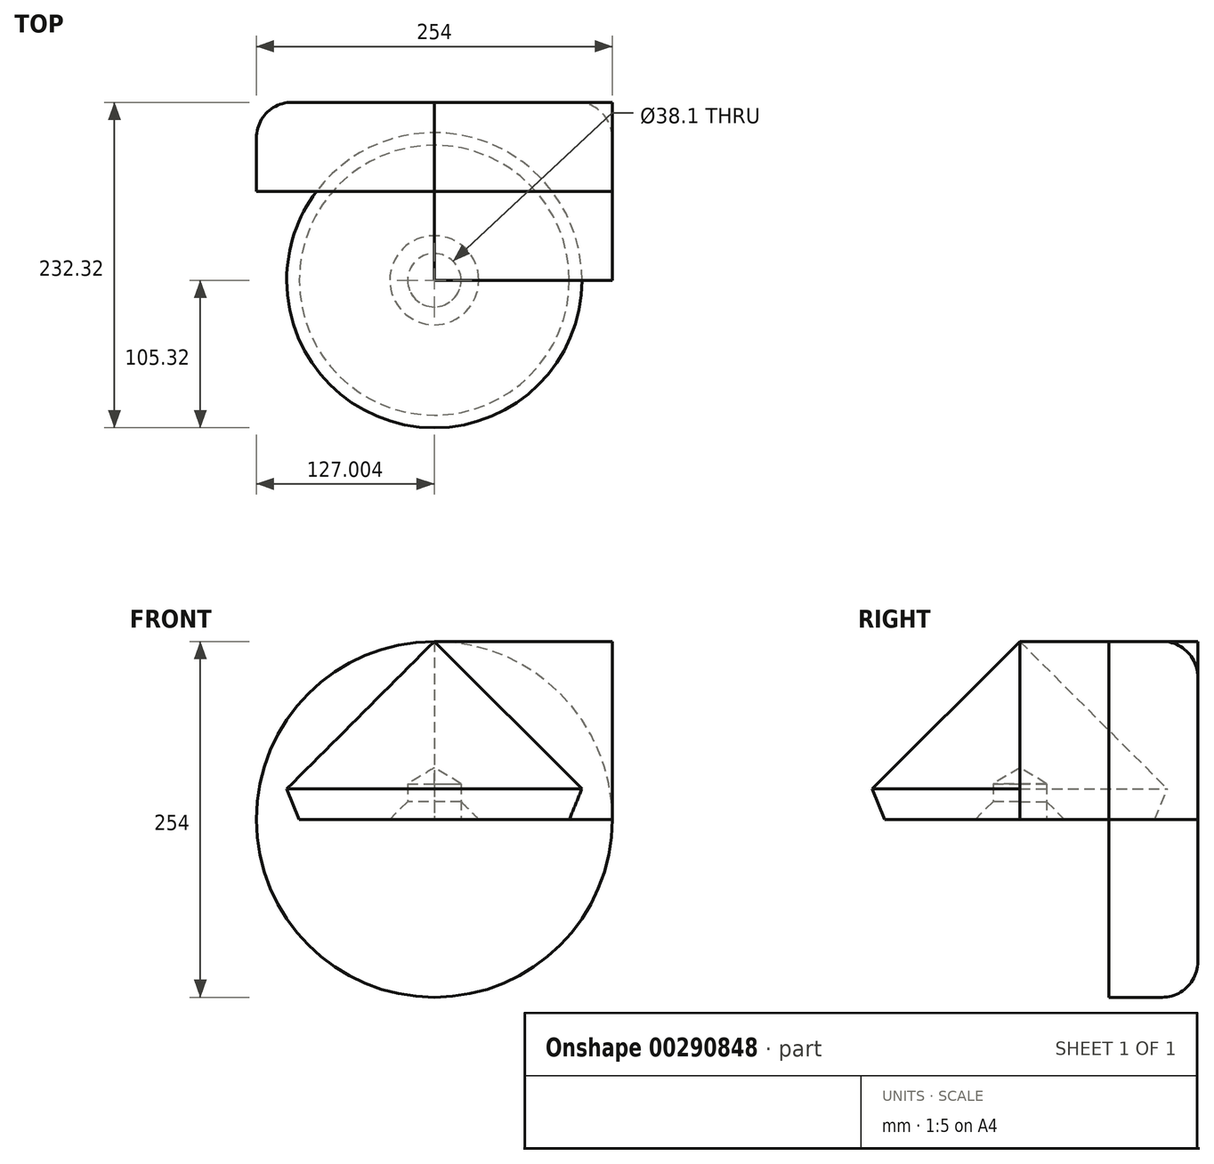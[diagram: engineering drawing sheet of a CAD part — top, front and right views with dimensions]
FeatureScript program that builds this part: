
annotation { "Feature Type Name" : "Feature", "Feature Type Description" : "" }
export const myFeature = defineFeature(function(context is Context, id is Id, definition is map)
    precondition{}
    {
        {
            var Q0;
            Q0=qCreatedBy(makeId("Front.planeOp"),FACE);
            var sketch = newSketch(context, id + "F0", { "sketchPlane" : qUnion([Q0])});
            skLineSegment(sketch, "E0.bottom", {"start": v(-69.47, 90.5) * mm, "end": v(57.53, 90.5) * mm});
            skLineSegment(sketch, "E0.top", {"start": v(-69.47, -36.5) * mm, "end": v(57.53, -36.5) * mm});
            skLineSegment(sketch, "E0.left", {"start": v(-69.47, 90.5) * mm, "end": v(-69.47, -36.5) * mm});
            skLineSegment(sketch, "E0.right", {"start": v(57.53, 90.5) * mm, "end": v(57.53, -36.5) * mm});
            skSolve(sketch);
        }
        {
            var Q0;
            Q0=makeQuery(id+"F0.imprint","IMPRINT",FACE,{"disambiguationData":[TD([[makeQuery(id+"F0.imprint","IMPRINT",EDGE,{"derivedFrom":sQuery(id+"F0.wireOp",EDGE,"E0.bottom")}),-1.0]])]});
            extrude(context, id + "F1", {"entities" : qUnion([Q0]), "depth" : 63.5 * mm, "hasSecondDirection" : true, "secondDirectionOppositeDirection" : true, "secondDirectionDepth" : 63.5 * mm});
        }
        {
            var Q0;
            Q0=makeQuery(id+"F1.opExtrude","SWEPT_FACE",FACE,{"disambiguationData":[OSD([sQuery(id+"F0.wireOp",EDGE,"E0.top")])]});
            var sketch = newSketch(context, id + "F2", { "sketchPlane" : qUnion([Q0])});
            skLineSegment(sketch, "E1", {"start": v(57.53, -63.5) * mm, "end": v(-69.47, 0) * mm, "construction": true});
            skLineSegment(sketch, "E2", {"start": v(57.53, 0) * mm, "end": v(-69.47, 0) * mm});
            skLineSegment(sketch, "E3", {"start": v(57.53, -63.5) * mm, "end": v(-69.47, -74.72) * mm});
            skLineSegment(sketch, "E4", {"start": v(-69.47, 0) * mm, "end": v(-69.47, -74.72) * mm});
            skSolve(sketch);
        }
        {
            var Q0;
            {var subQ0=sQuery(id+"F2.wireOp",EDGE,"E2");Q0=makeQuery(id+"F2.imprint","IMPRINT",FACE,{"disambiguationData":[TD([[makeQuery(id+"F2.imprint","IMPRINT",EDGE,{"derivedFrom":subQ0}),1.0]])]});}
            var Q1;
            Q1=sQuery(id+"F2.wireOp",EDGE,"E4");
            revolve(context, id + "F3", {"entities" : qUnion([Q0]), "axis" : qUnion([Q1]), "revolveType" : RevolveType.FULL});
        }
        {
            var Q0;
            Q0=makeQuery(id+"F1.opExtrude","CAP_FACE",FACE,{"disambiguationData":[OSD([sQuery(id+"F0.wireOp",EDGE,"E0.bottom"),sQuery(id+"F0.wireOp",EDGE,"E0.top"),sQuery(id+"F0.wireOp",EDGE,"E0.left"),sQuery(id+"F0.wireOp",EDGE,"E0.right")])],"isStart":false});
            var sketch = newSketch(context, id + "F4", { "sketchPlane" : qUnion([Q0])});
            skLineSegment(sketch, "E5", {"start": v(57.53, -36.5) * mm, "end": v(-69.47, 90.5) * mm});
            skLineSegment(sketch, "E6", {"start": v(-69.47, 90.5) * mm, "end": v(-69.47, -36.5) * mm});
            skLineSegment(sketch, "E7", {"start": v(-69.47, -36.5) * mm, "end": v(57.53, -36.5) * mm});
            skSolve(sketch);
        }
        {
            var Q0;
            Q0=makeQuery(id+"F4.imprint","IMPRINT",FACE,{"disambiguationData":[TD([[makeQuery(id+"F4.imprint","IMPRINT",EDGE,{"derivedFrom":sQuery(id+"F4.wireOp",EDGE,"E5")}),1.0]])]});
            var Q1;
            Q1=sQuery(id+"F4.wireOp",EDGE,"E6");
            revolve(context, id + "F5", {"entities" : qUnion([Q0]), "axis" : qUnion([Q1]), "revolveType" : RevolveType.FULL});
        }
        {
            var Q0;
            Q0=makeQuery(id+"F5.opRevolve","SWEPT_FACE",FACE,{"disambiguationData":[OSD([sQuery(id+"F4.wireOp",EDGE,"E7")])]});
            var sketch = newSketch(context, id + "F6", { "sketchPlane" : qUnion([Q0])});
            skCircle(sketch, "E8", {"center": v(-69.47, 63.5) * mm, "radius": 39.83 * mm});
            skSolve(sketch);
        }
        {
            var Q0;
            Q0=sQuery(id+"F6.wireOp",VERTEX,"E8.center");
            var Q1;
            Q1=makeQuery(id+"F1.opExtrude","SWEPT_BODY",BODY,{"disambiguationData":[OSD([sQuery(id+"F0.wireOp",EDGE,"E0.bottom"),sQuery(id+"F0.wireOp",EDGE,"E0.top"),sQuery(id+"F0.wireOp",EDGE,"E0.left"),sQuery(id+"F0.wireOp",EDGE,"E0.right")])]});
            var Q2;
            Q2=makeQuery(id+"F5.opRevolve","SWEPT_BODY",BODY,{"disambiguationData":[OSD([sQuery(id+"F4.wireOp",EDGE,"E5"),sQuery(id+"F4.wireOp",EDGE,"E6"),sQuery(id+"F4.wireOp",EDGE,"E7")])]});
            hole(context, id + "F7", {"style" : HoleStyle.SIMPLE, "endStyle" : HoleEndStyle.BLIND, "holeDiameter" : 38.1 * mm, "holeDepth" : 25.4 * mm, "tappedDepth" : 12.7 * mm, "tapClearance" : 3, "locations" : qUnion([Q0]), "scope" : qUnion([Q1, Q2])});
        }
        {
            var Q0;
            Q0=makeQuery(id+"F3.opRevolve","SWEPT_FACE",FACE,{"disambiguationData":[OSD([sQuery(id+"F0.wireOp",EDGE,"E0.top")])]});
            fillet(context, id + "F8", {"entities" : qUnion([Q0]), "radius" : 25.4 * mm, "tangentPropagation" : true, "allowEdgeOverflow" : false});
        }
        {
            var Q0;
            Q0=makeQuery(id+"F5.opRevolve","SWEPT_FACE",FACE,{"disambiguationData":[OSD([sQuery(id+"F4.wireOp",EDGE,"E7")])]});
            chamfer(context, id + "F9", {"entities" : qUnion([Q0]), "width" : 12.7 * mm, "tangentPropagation" : true});
        }
    });
